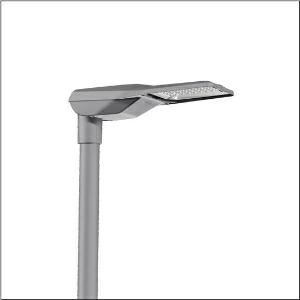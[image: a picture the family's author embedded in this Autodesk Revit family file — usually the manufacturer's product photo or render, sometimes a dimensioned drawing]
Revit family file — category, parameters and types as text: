
# Revit family: streetlight_sl_21_iq_mini___stw1_0a_5xe2e61g08hb_1142
name_source: partatom
category: Lighting Fixtures
units: mm (PartAtom-declared; Revit-internal decimal feet)

## family parameters
Cut with Voids When Loaded = No
Host = Face
Light Source = No
Part Type = Normal
Room Calculation Point = No
Round Connector Dimension = Use Diameter
Shared = No

## types (1)
- --- (1 x LED, 8480 lm, 70.9 W, 2700K)
    Apparent Load = 71 VA
    CIE Flux Codes = 38 75 98 100 100
    Color Rendering = 70
    Color Temperature = 2700K
    Default Elevation = 1800 mm
    Description = Streetlight SL 21 iQ mini, mast luminaire, primary light control with lens, of PMMA, primary optical cover: cover, of toughened safety glass, transparent, light distribution: STW1.0a, light emission: direct distribution, primary light characteristic: asymmetric, installation type: post-top, side-entry, LED, High Power LED, rated luminous flux: 8.480lm, luminous efficacy: 120lm/W, light colour: 727, colour temperature: 2700K, control: Street-Remote, Auto-Match, Temp-Guard, Lumen-Switch, Night-Set, Smart-Wire, Light-Fading, Desk-Remote (wireless, voltage-free reading and setting of iQ features in the workshop via application-optimized NFC function/RFID function), optimised constant luminous flux control (CLO 2.0), presetting dimming linear, mains connection: 220..240V, AC, 50/60Hz, start of lifetime: 71W, end of service life: 75W, reduction: 31W, luminaire housing, of diecast aluminium, powder-coated, Siteco® metallic grey (DB 702S), corrosivity category C5 mid according to DIN EN ISO 12944, please order mast flange separately, inclination adjustable: 0°, 5°, 10°, 15°, sealing non-destructively replaceable, multi-level sealing system, length: 628mm, width: 235mm, height: 110mm, mast flange for spigot size: 42mm (side-entry): 5XC10008XM4, 60/48mm (side-entry/post-top): 5XC10108XM2, 76/60mm (side-entry/post-top): 5XC10108XM1, protection rating (complete): IP66, insulation class (complete): insulation class II (safety insulation), certification: CE, ENEC, ENEC+, VDE, impact resistance: IK09, permissible operating ambient temperature for outdoor applications: -40..+50°C, standard-compliant lighting for roads and squares, packaging unit: 1 piece

Light Distribution: STW1.0a
    Height = 110 mm
    Lamp = 1 x LED
    Lamp Light Flux = 8480 lm
    Lamp Power = 70.9 W
    Lamp count = 1
    Length = 625 mm
    Luminous efficacy = 120 lm/W
    Manufacturer = Siteco
    ModVariant = No
    Model = 5XE2E61G08HB
    Number of Poles = 1
    OnlyDefault = Yes
    Power Factor = 1
    Product Name = Streetlight SL 21 iQ mini | STW1.0a
    Product group = mast luminaire | pylon top
    ProductGroupID = 6100
    Protection Class = Protection class II
    Protection Degree = IP 66
    RLX_Detail_Level = 1
    RLX_Emergency_Light_Flux = 0 lm
    RLX_Emergency_Type = 0
    RLX_Emergency_Type_DB = No
    RlxData = <blob elided: 92269 chars, md5=aee4d9b5>
    Socket = socket
    Standby Power = 0 W
    System Light Flux = 8480 lm
    System Power = 71 W
    Type Comments = factory setting: luminous flux: 100 % | dim-lin: 254 | 711 mA
    Type Image = l_1003519.jpg
    URL = http://relux.com
    VarID = @adj_090229
    Voltage = 0 V
    Weight = 0.00 kg
    Width = 234 mm

## geometry (parser evidence)
native form markers: Blend x4, Sweep x11
no freeform markers — native parametric forms only
